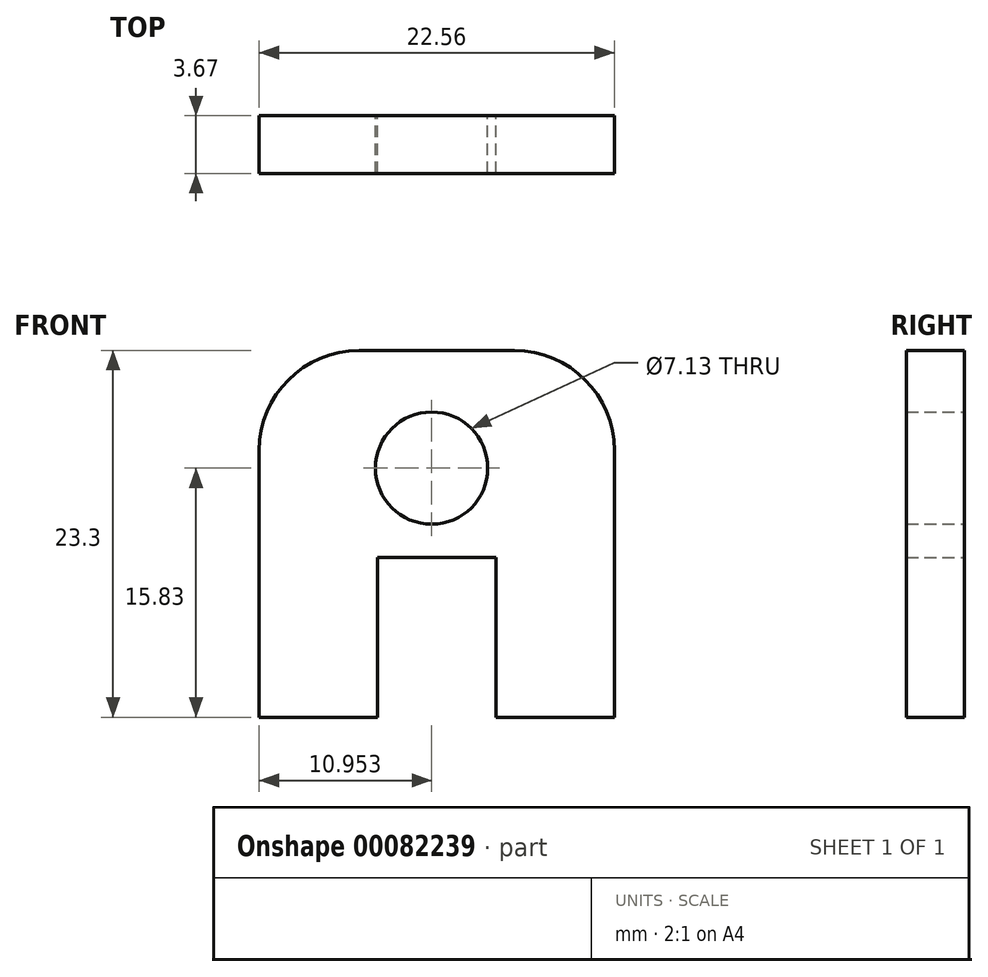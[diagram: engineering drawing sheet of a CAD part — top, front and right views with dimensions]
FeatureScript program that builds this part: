
annotation { "Feature Type Name" : "Feature", "Feature Type Description" : "" }
export const myFeature = defineFeature(function(context is Context, id is Id, definition is map)
    precondition{}
    {
        {
            var Q0;
            Q0=qCreatedBy(makeId("Front.planeOp"),FACE);
            var sketch = newSketch(context, id + "F0", { "sketchPlane" : qUnion([Q0])});
            skLineSegment(sketch, "E0", {"start": v(-57.98, 22.07) * mm, "end": v(-57.98, 32.23) * mm});
            skLineSegment(sketch, "E1", {"start": v(-57.98, 22.07) * mm, "end": v(-50.45, 22.07) * mm});
            skLineSegment(sketch, "E2", {"start": v(-50.45, 22.07) * mm, "end": v(-50.45, 32.23) * mm});
            skLineSegment(sketch, "E3", {"start": v(-50.45, 32.23) * mm, "end": v(-42.95, 32.23) * mm});
            skLineSegment(sketch, "E4", {"start": v(-42.95, 32.23) * mm, "end": v(-42.95, 22.07) * mm});
            skLineSegment(sketch, "E5", {"start": v(-42.95, 22.07) * mm, "end": v(-35.42, 22.07) * mm});
            skLineSegment(sketch, "E6", {"start": v(-35.42, 22.07) * mm, "end": v(-35.42, 32.23) * mm});
            skCircle(sketch, "E7", {"center": v(-47.03, 37.9) * mm, "radius": 3.56 * mm});
            skLineSegment(sketch, "E8", {"start": v(-57.98, 32.23) * mm, "end": v(-57.98, 39.02) * mm});
            skLineSegment(sketch, "E9", {"start": v(-35.42, 32.23) * mm, "end": v(-35.42, 39.02) * mm});
            skLineSegment(sketch, "E10", {"start": v(-51.63, 45.37) * mm, "end": v(-41.77, 45.37) * mm});
            skPoint(sketch, "E11.visualSharp", {"position": v(-57.98, 45.37) * mm});
            skArc(sketch, "E11.filletArc", {"start": v(-51.63, 45.37) * mm, "mid": v(-56.12, 43.5) * mm, "end": v(-57.98, 39.02) * mm});
            skPoint(sketch, "E12.visualSharp", {"position": v(-35.42, 45.37) * mm});
            skArc(sketch, "E12.filletArc", {"start": v(-35.42, 39.02) * mm, "mid": v(-37.28, 43.5) * mm, "end": v(-41.77, 45.37) * mm});
            skSolve(sketch);
        }
        {
            var Q0;
            Q0 = qSketchRegion(id + "F0", true);
            extrude(context, id + "F1", {"entities" : qUnion([Q0]), "depth" : 3.67 * mm});
        }
        {
            var Q0;
            Q0=makeQuery(id+"F1.opExtrude","CAP_FACE",FACE,{"disambiguationData":[OSD([sQuery(id+"F0.wireOp",EDGE,"E0"),sQuery(id+"F0.wireOp",EDGE,"E1"),sQuery(id+"F0.wireOp",EDGE,"E2"),sQuery(id+"F0.wireOp",EDGE,"E3"),sQuery(id+"F0.wireOp",EDGE,"E4"),sQuery(id+"F0.wireOp",EDGE,"E5"),sQuery(id+"F0.wireOp",EDGE,"E6"),sQuery(id+"F0.wireOp",EDGE,"PB0XEi1j-penY-tP5V-zynO-Uonu9r0ZYpvE"),sQuery(id+"F0.wireOp",EDGE,"IkhPvFyX-KMYA-b2E6-6VNL-dsly9mBgN7en"),sQuery(id+"F0.wireOp",EDGE,"12zk7uNB-OPWN-0kTp-xzUF-lMa6TqQoNE3d"),sQuery(id+"F0.wireOp",EDGE,"cutx4Zy8-8hFI-2iSH-hRR9-y9QQ5rqyXNZF"),sQuery(id+"F0.wireOp",EDGE,"a7CxpQ3t-GiMn-doa5-GgJ1-iMbd9YbXyr8i"),sQuery(id+"F0.wireOp",EDGE,"E7")])],"isStart":false});
            var sketch = newSketch(context, id + "F2", { "sketchPlane" : qUnion([Q0])});
            skLineSegment(sketch, "E13", {"start": v(-57.98, 22.07) * mm, "end": v(-57.98, 38.32) * mm});
            skLineSegment(sketch, "E14", {"start": v(-57.98, 38.32) * mm, "end": v(-64.34, 38.32) * mm});
            skLineSegment(sketch, "E15", {"start": v(-64.34, 38.32) * mm, "end": v(-64.34, 22.07) * mm});
            skLineSegment(sketch, "E16", {"start": v(-64.34, 22.07) * mm, "end": v(-57.98, 22.07) * mm});
            skLineSegment(sketch, "E17", {"start": v(-35.42, 22.07) * mm, "end": v(-35.42, 38.32) * mm});
            skLineSegment(sketch, "E18", {"start": v(-35.42, 38.32) * mm, "end": v(-28.54, 38.32) * mm});
            skLineSegment(sketch, "E19", {"start": v(-28.54, 38.32) * mm, "end": v(-28.54, 22.07) * mm});
            skLineSegment(sketch, "E20", {"start": v(-28.54, 22.07) * mm, "end": v(-35.42, 22.07) * mm});
            skSolve(sketch);
        }
        {
            var Q0;
            Q0 = qSketchRegion(id + "F2", true);
            extrude(context, id + "F3", {"entities" : qUnion([Q0]), "operationType" : NewBodyOperationType.REMOVE, "endBound" : BoundingType.THROUGH_ALL, "oppositeDirection" : true, "depth" : 25.4 * mm});
        }
    });
